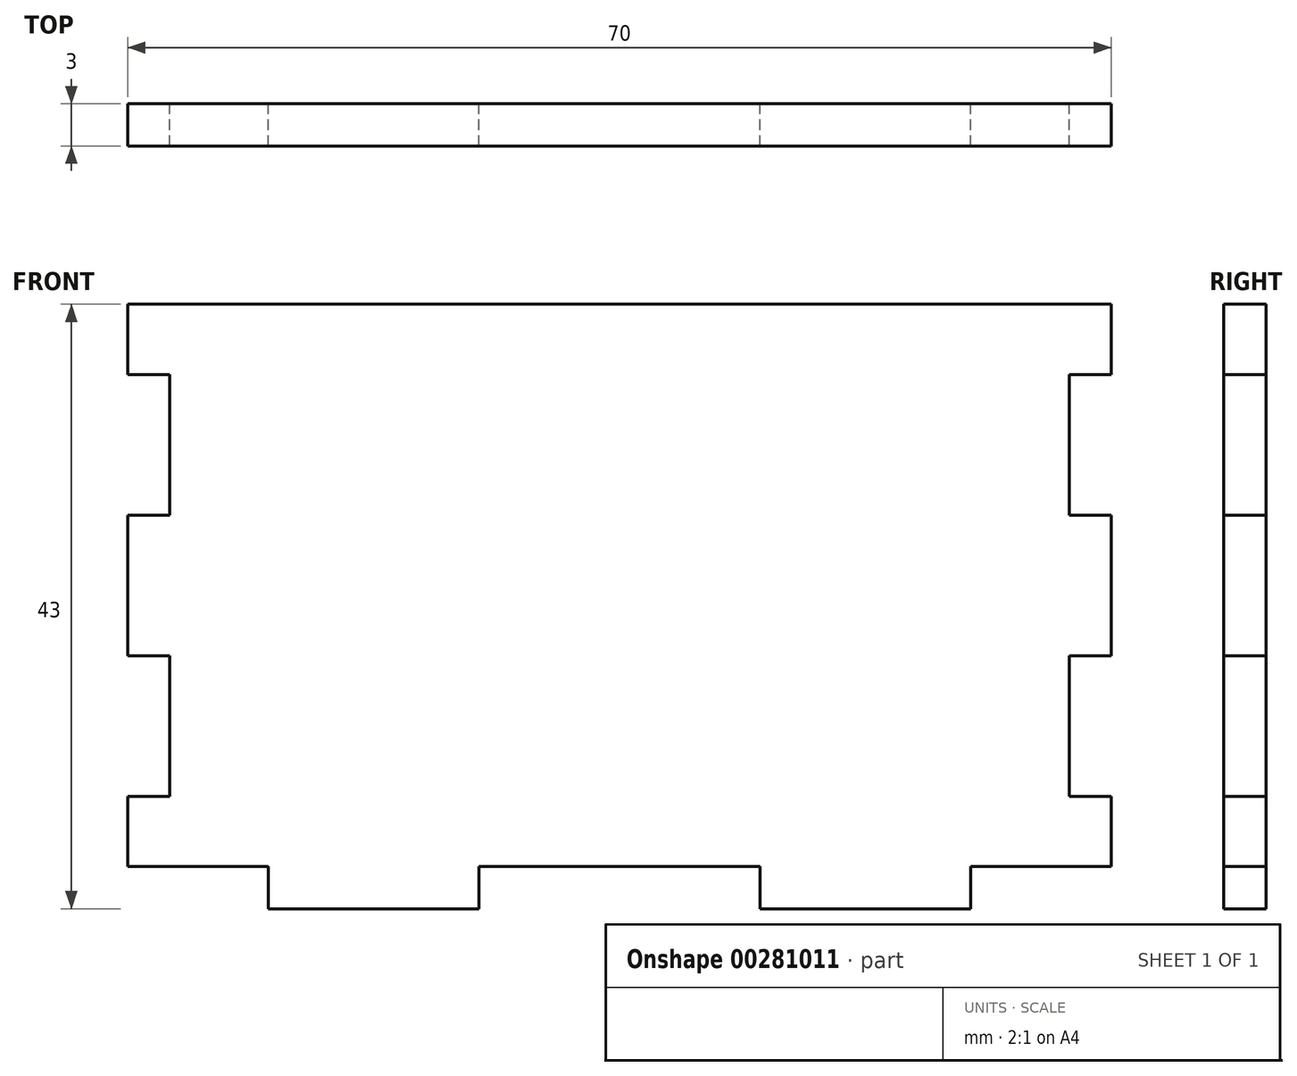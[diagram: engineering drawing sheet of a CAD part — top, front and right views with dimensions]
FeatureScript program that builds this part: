
annotation { "Feature Type Name" : "Feature", "Feature Type Description" : "" }
export const myFeature = defineFeature(function(context is Context, id is Id, definition is map)
    precondition{}
    {
        {
            var Q0;
            Q0=qCreatedBy(makeId("Front.planeOp"),FACE);
            var sketch = newSketch(context, id + "F0", { "sketchPlane" : qUnion([Q0])});
            skLineSegment(sketch, "E0.bottom", {"start": v(35, -20) * mm, "end": v(25, -20) * mm});
            skLineSegment(sketch, "E0.top", {"start": v(35, 20) * mm, "end": v(-35, 20) * mm});
            skLineSegment(sketch, "E0.right", {"start": v(-35, -20) * mm, "end": v(-35, -15) * mm});
            skPoint(sketch, "E0.middle", {"position": v(0, 0) * mm});
            skLineSegment(sketch, "E1.top", {"start": v(-10, -23) * mm, "end": v(-25, -23) * mm});
            skLineSegment(sketch, "E1.left", {"start": v(-10, -20) * mm, "end": v(-10, -23) * mm});
            skLineSegment(sketch, "E1.right", {"start": v(-25, -20) * mm, "end": v(-25, -23) * mm});
            skLineSegment(sketch, "E2.top", {"start": v(10, -23) * mm, "end": v(25, -23) * mm});
            skLineSegment(sketch, "E2.left", {"start": v(10, -20) * mm, "end": v(10, -23) * mm});
            skLineSegment(sketch, "E2.right", {"start": v(25, -20) * mm, "end": v(25, -23) * mm});
            skLineSegment(sketch, "E3.trimOffspring", {"start": v(-25, -20) * mm, "end": v(-35, -20) * mm});
            skLineSegment(sketch, "E4.trimOffspring", {"start": v(10, -20) * mm, "end": v(-10, -20) * mm});
            skLineSegment(sketch, "E5.bottom", {"start": v(-35, 15) * mm, "end": v(-32, 15) * mm});
            skLineSegment(sketch, "E5.top", {"start": v(-35, 5) * mm, "end": v(-32, 5) * mm});
            skLineSegment(sketch, "E5.right", {"start": v(-32, 15) * mm, "end": v(-32, 5) * mm});
            skLineSegment(sketch, "E6.bottom", {"start": v(-35, -5) * mm, "end": v(-32, -5) * mm});
            skLineSegment(sketch, "E6.top", {"start": v(-35, -15) * mm, "end": v(-32, -15) * mm});
            skLineSegment(sketch, "E6.right", {"start": v(-32, -5) * mm, "end": v(-32, -15) * mm});
            skLineSegment(sketch, "E7.trimOffspring", {"start": v(-35, 15) * mm, "end": v(-35, 20) * mm});
            skLineSegment(sketch, "E8.trimOffspring", {"start": v(-35, -5) * mm, "end": v(-35, 5) * mm});
            skLineSegment(sketch, "E9.MirrorCS", {"start": v(35, 5) * mm, "end": v(32, 5) * mm});
            skLineSegment(sketch, "E10.MirrorCS", {"start": v(35, 15) * mm, "end": v(32, 15) * mm});
            skLineSegment(sketch, "E11.MirrorCS", {"start": v(35, -5) * mm, "end": v(32, -5) * mm});
            skLineSegment(sketch, "E12.MirrorCS", {"start": v(35, -15) * mm, "end": v(32, -15) * mm});
            skLineSegment(sketch, "E13.MirrorCS", {"start": v(35, -5) * mm, "end": v(35, 5) * mm});
            skLineSegment(sketch, "E14.MirrorCS", {"start": v(32, -5) * mm, "end": v(32, -15) * mm});
            skLineSegment(sketch, "E15.MirrorCS", {"start": v(32, 15) * mm, "end": v(32, 5) * mm});
            skLineSegment(sketch, "E16.MirrorCS", {"start": v(35, 15) * mm, "end": v(35, 20) * mm});
            skLineSegment(sketch, "E17.MirrorCS", {"start": v(35, -20) * mm, "end": v(35, -15) * mm});
            skSolve(sketch);
        }
        {
            var Q0;
            Q0 = qSketchRegion(id + "F0", true);
            extrude(context, id + "F1", {"entities" : qUnion([Q0]), "depth" : 3 * mm});
        }
    });
